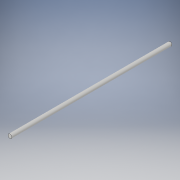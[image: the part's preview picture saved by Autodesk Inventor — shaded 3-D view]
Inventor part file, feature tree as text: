
AUTODESK INVENTOR PART (.ipt)
format: ipt  version: 2019 (Build 230136000, 136)  size: 90,624 bytes
history: native  units: mm
features: extrude x1, sketch x1
ambient origin geometry x8: Origin, YZ Plane, XZ Plane, XY Plane, X Axis, Y Axis, Z Axis, Center Point
bodies: Solid1 (feature_tree)
feature tree (2):
  extrude  "Extrusion1"  Depth=620.0mm TaperAngle=0.0deg
  sketch  "Sketch1"  dims[d0=15.0mm d1=620.0mm d2=0.0mm]
